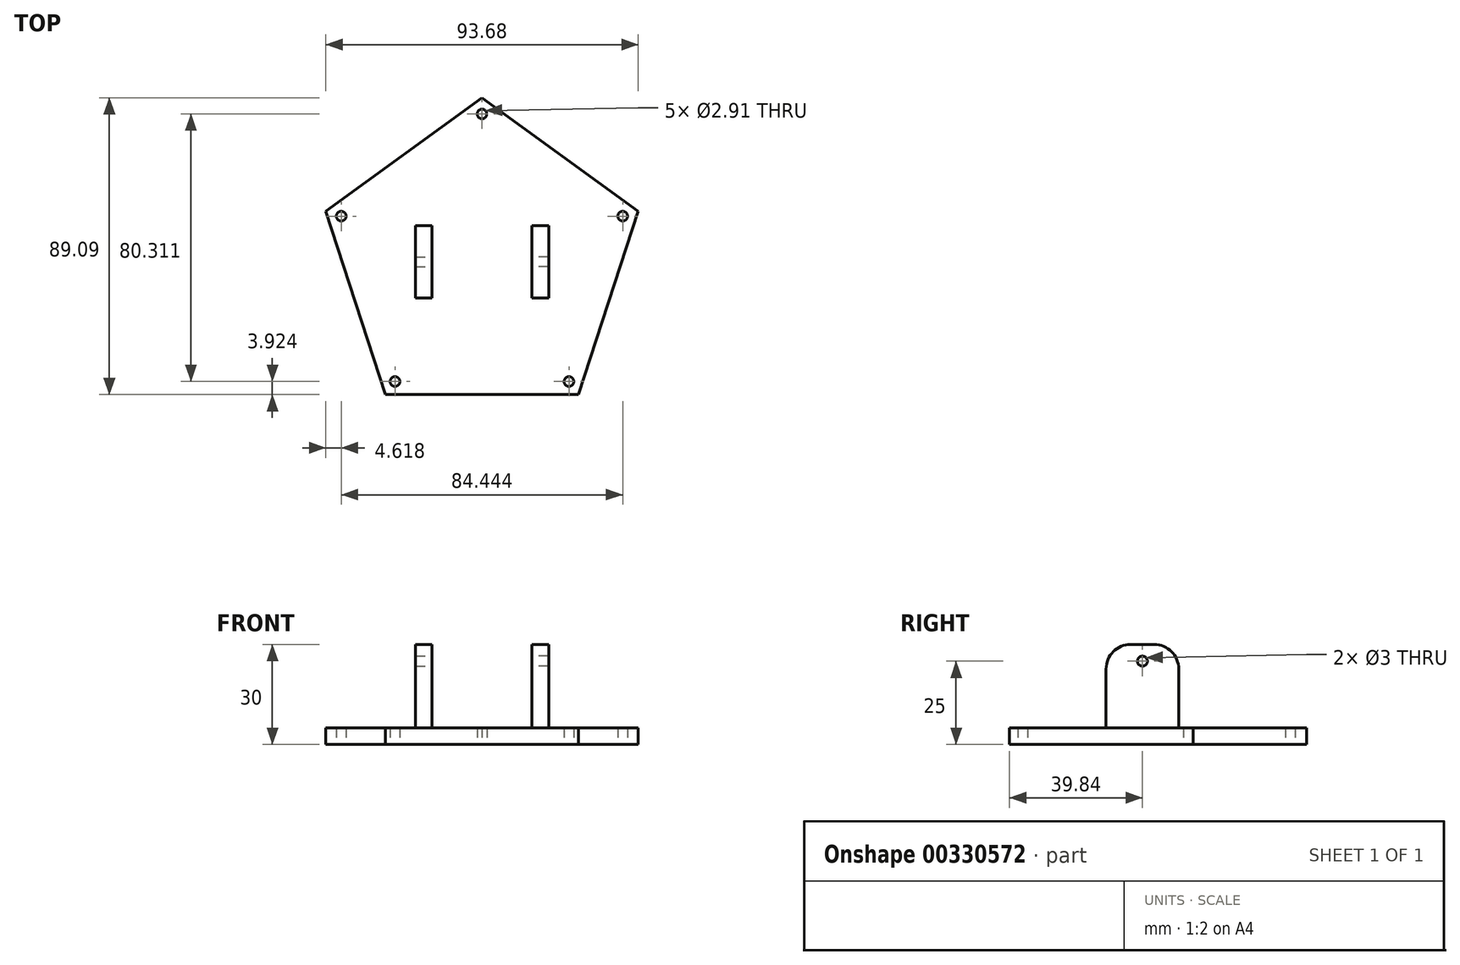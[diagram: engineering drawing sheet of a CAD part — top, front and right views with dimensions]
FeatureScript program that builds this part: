
annotation { "Feature Type Name" : "Feature", "Feature Type Description" : "" }
export const myFeature = defineFeature(function(context is Context, id is Id, definition is map)
    precondition{}
    {
        {
            var Q0;
            Q0=qCreatedBy(makeId("Top.planeOp"),FACE);
            var sketch = newSketch(context, id + "F0", { "sketchPlane" : qUnion([Q0])});
            skCircle(sketch, "E0.cCircle", {"center": v(0, 0) * mm, "radius": 39.84 * mm, "construction": true});
            skLineSegment(sketch, "E0.0", {"start": v(0, 49.25) * mm, "end": v(46.84, 15.22) * mm});
            skLineSegment(sketch, "E0.1", {"start": v(46.84, 15.22) * mm, "end": v(28.95, -39.84) * mm});
            skLineSegment(sketch, "E0.2", {"start": v(28.95, -39.84) * mm, "end": v(-28.95, -39.84) * mm});
            skLineSegment(sketch, "E0.3", {"start": v(-28.95, -39.84) * mm, "end": v(-46.84, 15.22) * mm});
            skLineSegment(sketch, "E0.4", {"start": v(-46.84, 15.22) * mm, "end": v(0, 49.25) * mm});
            skPoint(sketch, "E0.0.midPoint", {"position": v(23.42, 32.23) * mm});
            skCircle(sketch, "E1", {"center": v(0, 44.4) * mm, "radius": 1.45 * mm});
            skCircle(sketch, "E2.1.0", {"center": v(-42.22, 13.72) * mm, "radius": 1.45 * mm});
            skCircle(sketch, "E2.2.0", {"center": v(-26.1, -35.92) * mm, "radius": 1.45 * mm});
            skCircle(sketch, "E2.3.0", {"center": v(26.1, -35.92) * mm, "radius": 1.45 * mm});
            skCircle(sketch, "E2.4.0", {"center": v(42.22, 13.72) * mm, "radius": 1.45 * mm});
            skLineSegment(sketch, "E3.left", {"start": v(-20, 10.9) * mm, "end": v(-20, -10.9) * mm});
            skLineSegment(sketch, "E3.right", {"start": v(20, 10.9) * mm, "end": v(20, -10.9) * mm});
            skLineSegment(sketch, "E4", {"start": v(-15, 10.9) * mm, "end": v(-15, -10.9) * mm});
            skLineSegment(sketch, "E5", {"start": v(15, 10.9) * mm, "end": v(15, -10.9) * mm});
            skLineSegment(sketch, "E6", {"start": v(-20, 10.9) * mm, "end": v(-15, 10.9) * mm});
            skLineSegment(sketch, "E7", {"start": v(15, 10.9) * mm, "end": v(20, 10.9) * mm});
            skLineSegment(sketch, "E8", {"start": v(20, -10.9) * mm, "end": v(15, -10.9) * mm});
            skLineSegment(sketch, "E9", {"start": v(-15, -10.9) * mm, "end": v(-20, -10.9) * mm});
            skSolve(sketch);
        }
        {
            var Q0;
            Q0=makeQuery(id+"F0.imprint","IMPRINT",FACE,{"disambiguationData":[TD([[makeQuery(id+"F0.imprint","IMPRINT",EDGE,{"derivedFrom":sQuery(id+"F0.wireOp",EDGE,"E0.0")}),-1.0]])]});
            extrude(context, id + "F1", {"entities" : qUnion([Q0]), "depth" : 5 * mm});
        }
        {
            var Q0;
            Q0=makeQuery(id+"F0.imprint","IMPRINT",FACE,{"disambiguationData":[TD([[makeQuery(id+"F0.imprint","IMPRINT",EDGE,{"derivedFrom":sQuery(id+"F0.wireOp",EDGE,"E3.left")}),1.0]])]});
            var Q1;
            Q1=makeQuery(id+"F0.imprint","IMPRINT",FACE,{"disambiguationData":[TD([[makeQuery(id+"F0.imprint","IMPRINT",EDGE,{"derivedFrom":sQuery(id+"F0.wireOp",EDGE,"E3.right")}),-1.0]])]});
            extrude(context, id + "F2", {"entities" : qUnion([Q0, Q1]), "operationType" : NewBodyOperationType.ADD, "depth" : 30 * mm});
        }
        {
            var Q0;
            Q0=makeQuery(id+"F2.opExtrude","CAP_EDGE",EDGE,{"disambiguationData":[OSD([sQuery(id+"F0.wireOp",EDGE,"E9")])],"isStart":false});
            var Q1;
            Q1=makeQuery(id+"F2.opExtrude","CAP_EDGE",EDGE,{"disambiguationData":[OSD([sQuery(id+"F0.wireOp",EDGE,"E8")])],"isStart":false});
            var Q2;
            Q2=makeQuery(id+"F2.opExtrude","CAP_EDGE",EDGE,{"disambiguationData":[OSD([sQuery(id+"F0.wireOp",EDGE,"E7")])],"isStart":false});
            var Q3;
            Q3=makeQuery(id+"F2.opExtrude","CAP_EDGE",EDGE,{"disambiguationData":[OSD([sQuery(id+"F0.wireOp",EDGE,"E6")])],"isStart":false});
            fillet(context, id + "F3", {"entities" : qUnion([Q0, Q1, Q2, Q3]), "radius" : 7.36 * mm, "tangentPropagation" : true, "allowEdgeOverflow" : false});
        }
        {
            var Q0;
            Q0=qCreatedBy(makeId("Right.planeOp"),FACE);
            var sketch = newSketch(context, id + "F4", { "sketchPlane" : qUnion([Q0])});
            skPoint(sketch, "E10", {"position": v(0, 25) * mm});
            skSolve(sketch);
        }
        {
            var Q0;
            Q0=sQuery(id+"F4.wireOp",VERTEX,"E10");
            var Q1;
            Q1=makeQuery(id+"F1.opExtrude","SWEPT_BODY",BODY,{"disambiguationData":[OSD([sQuery(id+"F0.wireOp",EDGE,"E0.0"),sQuery(id+"F0.wireOp",EDGE,"E0.1"),sQuery(id+"F0.wireOp",EDGE,"E0.2"),sQuery(id+"F0.wireOp",EDGE,"E0.3"),sQuery(id+"F0.wireOp",EDGE,"E0.4"),sQuery(id+"F0.wireOp",EDGE,"E1"),sQuery(id+"F0.wireOp",EDGE,"E2.1.0"),sQuery(id+"F0.wireOp",EDGE,"E2.2.0"),sQuery(id+"F0.wireOp",EDGE,"E2.3.0"),sQuery(id+"F0.wireOp",EDGE,"E2.4.0"),sQuery(id+"F0.wireOp",EDGE,"E3.left"),sQuery(id+"F0.wireOp",EDGE,"E3.right"),sQuery(id+"F0.wireOp",EDGE,"E4"),sQuery(id+"F0.wireOp",EDGE,"E5"),sQuery(id+"F0.wireOp",EDGE,"E6"),sQuery(id+"F0.wireOp",EDGE,"E7"),sQuery(id+"F0.wireOp",EDGE,"E8"),sQuery(id+"F0.wireOp",EDGE,"E9")])]});
            hole(context, id + "F5", {"style" : HoleStyle.SIMPLE, "endStyle" : HoleEndStyle.BLIND, "oppositeDirection" : true, "holeDiameter" : 3 * mm, "holeDepth" : 100 * mm, "tappedDepth" : 12.7 * mm, "tapClearance" : 3, "locations" : qUnion([Q0]), "scope" : qUnion([Q1])});
        }
        {
            var Q0;
            Q0=sQuery(id+"F4.wireOp",VERTEX,"E10");
            var Q1;
            Q1=makeQuery(id+"F1.opExtrude","SWEPT_BODY",BODY,{"disambiguationData":[OSD([sQuery(id+"F0.wireOp",EDGE,"E0.0"),sQuery(id+"F0.wireOp",EDGE,"E0.1"),sQuery(id+"F0.wireOp",EDGE,"E0.2"),sQuery(id+"F0.wireOp",EDGE,"E0.3"),sQuery(id+"F0.wireOp",EDGE,"E0.4"),sQuery(id+"F0.wireOp",EDGE,"E1"),sQuery(id+"F0.wireOp",EDGE,"E2.1.0"),sQuery(id+"F0.wireOp",EDGE,"E2.2.0"),sQuery(id+"F0.wireOp",EDGE,"E2.3.0"),sQuery(id+"F0.wireOp",EDGE,"E2.4.0"),sQuery(id+"F0.wireOp",EDGE,"E3.left"),sQuery(id+"F0.wireOp",EDGE,"E3.right"),sQuery(id+"F0.wireOp",EDGE,"E4"),sQuery(id+"F0.wireOp",EDGE,"E5"),sQuery(id+"F0.wireOp",EDGE,"E6"),sQuery(id+"F0.wireOp",EDGE,"E7"),sQuery(id+"F0.wireOp",EDGE,"E8"),sQuery(id+"F0.wireOp",EDGE,"E9")])]});
            hole(context, id + "F6", {"style" : HoleStyle.SIMPLE, "endStyle" : HoleEndStyle.BLIND, "holeDiameter" : 3 * mm, "holeDepth" : 100 * mm, "tappedDepth" : 12.7 * mm, "tapClearance" : 3, "locations" : qUnion([Q0]), "scope" : qUnion([Q1])});
        }
    });
